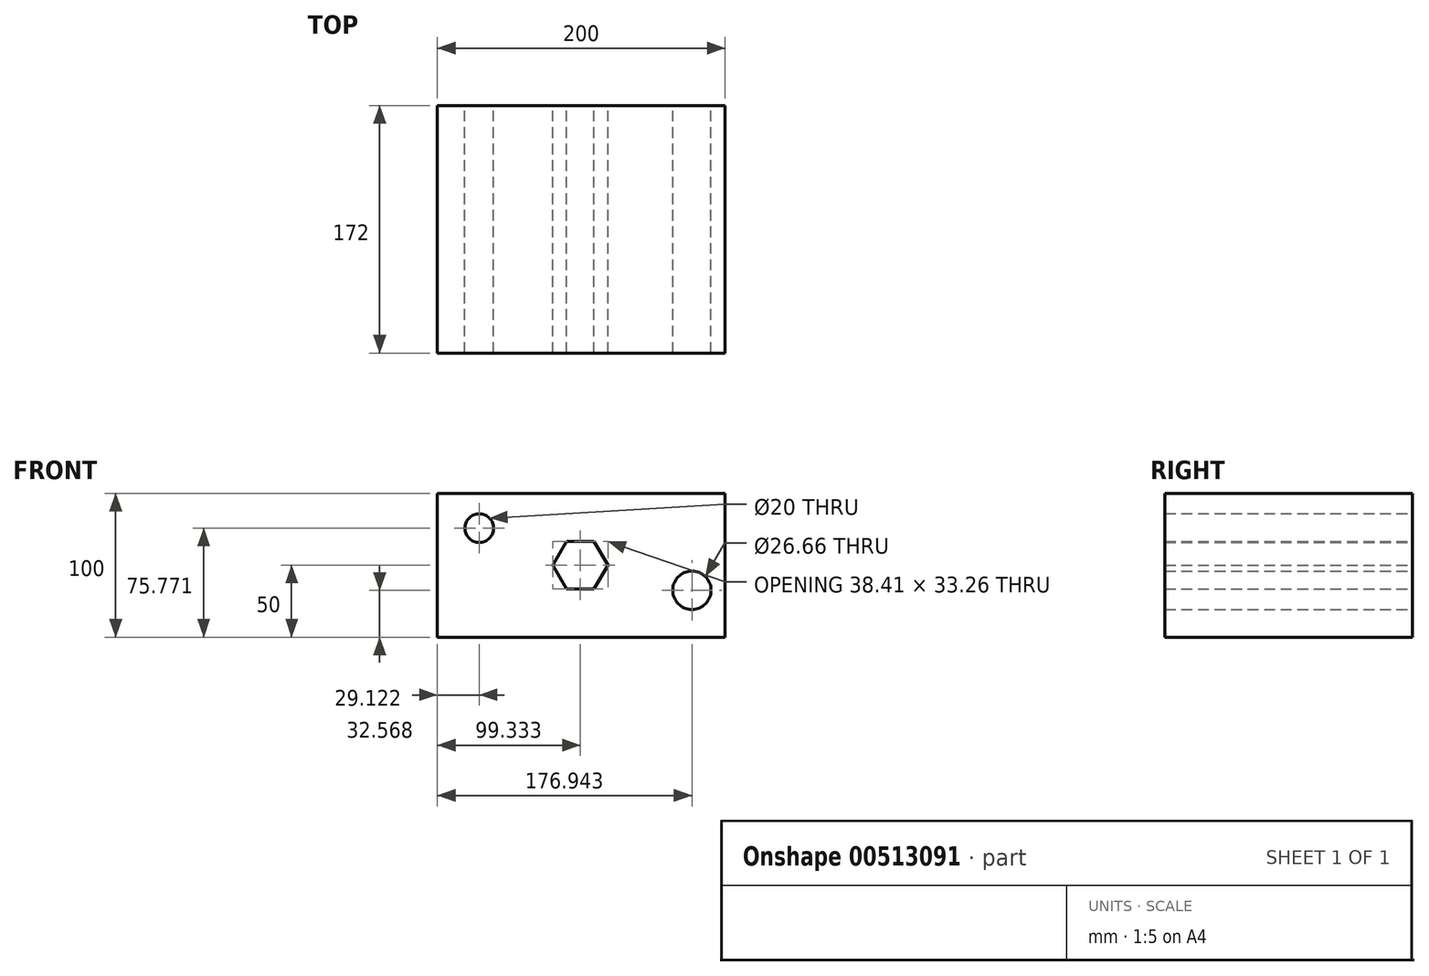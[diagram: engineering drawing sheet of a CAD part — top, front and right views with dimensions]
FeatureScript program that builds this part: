
annotation { "Feature Type Name" : "Feature", "Feature Type Description" : "" }
export const myFeature = defineFeature(function(context is Context, id is Id, definition is map)
    precondition{}
    {
        {
            var Q0;
            Q0=qCreatedBy(makeId("Front.planeOp"),FACE);
            var sketch = newSketch(context, id + "F0", { "sketchPlane" : qUnion([Q0])});
            skLineSegment(sketch, "E0.bottom", {"start": v(0, 0) * mm, "end": v(200, 0) * mm});
            skLineSegment(sketch, "E0.top", {"start": v(0, -100) * mm, "end": v(200, -100) * mm});
            skLineSegment(sketch, "E0.left", {"start": v(0, 0) * mm, "end": v(0, -100) * mm});
            skLineSegment(sketch, "E0.right", {"start": v(200, 0) * mm, "end": v(200, -100) * mm});
            skCircle(sketch, "E1", {"center": v(29.12, -24.23) * mm, "radius": 10 * mm});
            skCircle(sketch, "E2", {"center": v(176.94, -67.43) * mm, "radius": 13.33 * mm});
            skCircle(sketch, "E3.cCircle", {"center": v(99.33, -50) * mm, "radius": 16.63 * mm, "construction": true});
            skPoint(sketch, "E3.cCircle.centerSnap0", {"position": v(0, -50) * mm});
            skLineSegment(sketch, "E3.0", {"start": v(89.73, -33.37) * mm, "end": v(108.94, -33.37) * mm});
            skLineSegment(sketch, "E3.1", {"start": v(108.94, -33.37) * mm, "end": v(118.54, -50) * mm});
            skLineSegment(sketch, "E3.2", {"start": v(118.54, -50) * mm, "end": v(108.94, -66.63) * mm});
            skLineSegment(sketch, "E3.3", {"start": v(108.94, -66.63) * mm, "end": v(89.73, -66.63) * mm});
            skLineSegment(sketch, "E3.4", {"start": v(89.73, -66.63) * mm, "end": v(80.13, -50) * mm});
            skLineSegment(sketch, "E3.5", {"start": v(80.13, -50) * mm, "end": v(89.73, -33.37) * mm});
            skPoint(sketch, "E3.0.midPoint", {"position": v(99.33, -33.37) * mm});
            skSolve(sketch);
        }
        {
            var Q0;
            Q0 = qSketchRegion(id + "F0", true);
            extrude(context, id + "F1", {"entities" : qUnion([Q0]), "depth" : 172 * mm});
        }
    });
